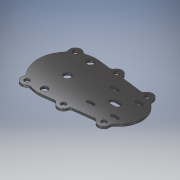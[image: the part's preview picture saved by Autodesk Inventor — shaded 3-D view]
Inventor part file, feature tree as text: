
AUTODESK INVENTOR PART (.ipt)
format: ipt  version: 2017 (Build 210142000, 142)  size: 290,304 bytes
history: native  units: mm
features: extrude x4, sketch x4, other x1, fillet x1
ambient origin geometry x8: Origin, YZ Plane, XZ Plane, XY Plane, X Axis, Y Axis, Z Axis, Center Point
bodies: Body1 (feature_tree)
feature tree (10):
  other  "Sólido1"
  extrude  "Extrusión1"  Depth=88.9mm
  extrude  "Extrusión2"  Depth=22.225mm
  fillet  "Empalme1"  Radius=22.225mm
  extrude  "Extrusión3"  Depth=22.225mm
  extrude  "Extrusión4"  TaperAngle=0.0deg  [1 undecoded]
  sketch  "Boceto1"  dims[d0=114.3mm d1=88.9mm]
  sketch  "Boceto2"  dims[d2=203.2mm d3=22.225mm d4=22.225mm]
  sketch  "Boceto3"  dims[d7=22.225mm d8=22.225mm]
  sketch  "Boceto4"  dims[d11=22.225mm d13=0.0mm d14=22.225mm d16=4.445mm d17=0.0mm d18=9.525mm d19=9.525mm d20=9.525mm d21=9.525mm d22=9.525mm d23=9.525mm d24=25.4mm d25=0.0mm d26=6.35mm d27=12.7mm d28=12.7mm d29=44.45mm d30=44.45mm d31=31.75mm d32=31.75mm d33=14.2875mm d34=12.7mm d35=12.7mm d36=45.0mm d37=45.0mm d38=25.4mm d39=0.0mm d40=11.1125mm d41=56.0mm d42=56.0mm d43=28.0mm d44=28.0mm d45=0.0mm d46=93.4212mm d47=47.5mm d48=47.5mm d49=23.75mm d50=23.75mm d57=5.55625mm d58=5.159375mm d59=5.55625mm d60=5.55625mm d61=5.159375mm d62=5.159375mm d63=5.55625mm d64=5.159375mm d65=0.0mm d66=5.55625mm d67=5.55625mm d68=5.159375mm d69=5.159375mm d70=0.0mm d71=5.55625mm d72=5.55625mm d73=5.159375mm d74=5.159375mm d75=0.0mm d76=25.4mm d77=0.0mm d78=11.1125mm d79=11.1125mm d80=5.159375mm d81=5.159375mm]
note: 1 required parameter value undecoded (feature->parameter linkage not recoverable at this tier; creation-order binding heuristic only, values carry confidence <= 0.55)
